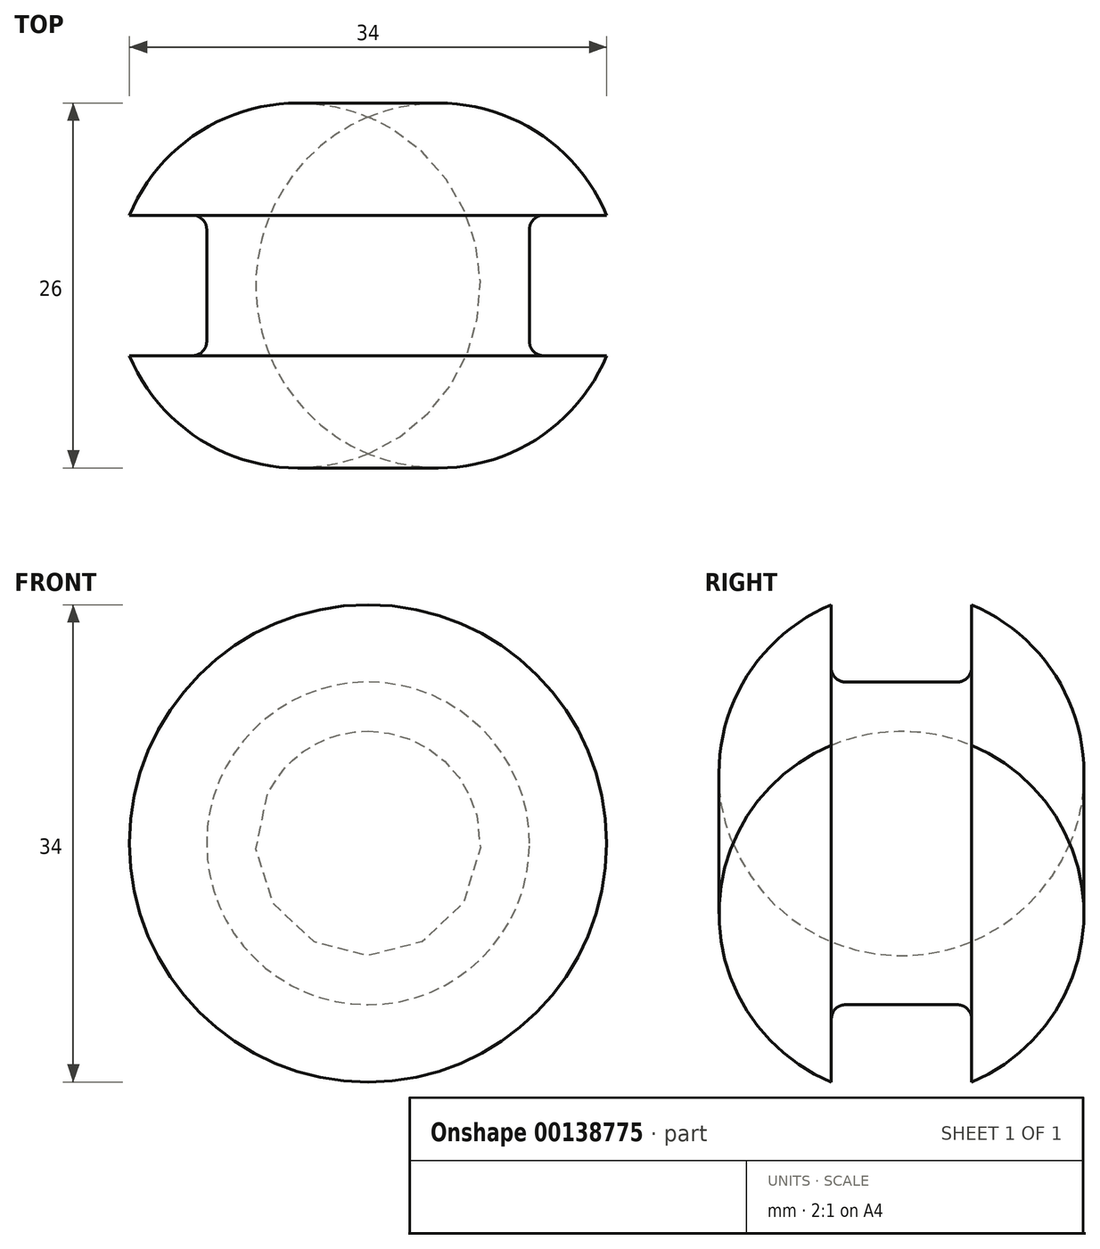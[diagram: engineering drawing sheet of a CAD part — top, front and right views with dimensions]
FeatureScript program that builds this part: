
annotation { "Feature Type Name" : "Feature", "Feature Type Description" : "" }
export const myFeature = defineFeature(function(context is Context, id is Id, definition is map)
    precondition{}
    {
        {
            var Q0;
            Q0=qCreatedBy(makeId("Right.planeOp"),FACE);
            var sketch = newSketch(context, id + "F0", { "sketchPlane" : qUnion([Q0])});
            skLineSegment(sketch, "E0.bottom", {"start": v(5, 17) * mm, "end": v(-5, 17) * mm, "construction": true});
            skLineSegment(sketch, "E0.top", {"start": v(5, 11.5) * mm, "end": v(-5, 11.5) * mm});
            skLineSegment(sketch, "E0.left", {"start": v(5, 17) * mm, "end": v(5, 11.5) * mm});
            skLineSegment(sketch, "E0.right", {"start": v(-5, 17) * mm, "end": v(-5, 11.5) * mm});
            skPoint(sketch, "E0.middle", {"position": v(0, 14.25) * mm});
            skLineSegment(sketch, "E1", {"start": v(0, 11.5) * mm, "end": v(0, 18) * mm, "construction": true});
            skPoint(sketch, "E1.endSnap0", {"position": v(0, 11.5) * mm});
            skArc(sketch, "E2", {"start": v(5, 17) * mm, "mid": v(0, 18) * mm, "end": v(-5, 17) * mm});
            skLineSegment(sketch, "E3", {"start": v(-5, 0) * mm, "end": v(5, 0) * mm});
            skSolve(sketch);
        }
        {
            var Q0;
            Q0=makeQuery(id+"F0.imprint","IMPRINT",FACE,{"disambiguationData":[TD([[makeQuery(id+"F0.imprint","IMPRINT",EDGE,{"derivedFrom":sQuery(id+"F0.wireOp",EDGE,"E0.top")}),-1.0]])]});
            var Q1;
            Q1=sQuery(id+"F0.wireOp",EDGE,"E3");
            revolve(context, id + "F1", {"entities" : qUnion([Q0]), "axis" : qUnion([Q1]), "revolveType" : RevolveType.FULL});
        }
        {
            var Q0;
            Q0=makeQuery(id+"F1.opRevolve","SWEPT_FACE",FACE,{"disambiguationData":[OSD([sQuery(id+"F0.wireOp",EDGE,"E0.top")])]});
            var Q1;
            Q1=makeQuery(id+"F1.opRevolve","SWEPT_EDGE",EDGE,{"disambiguationData":[OSD([sQuery(id+"F0.wireOp",EDGE,"E0.top"),sQuery(id+"F0.wireOp",EDGE,"E0.right")])]});
            fillet(context, id + "F2", {"entities" : qUnion([Q0, Q1]), "radius" : 1 * mm, "tangentPropagation" : true, "allowEdgeOverflow" : false});
        }
    });
